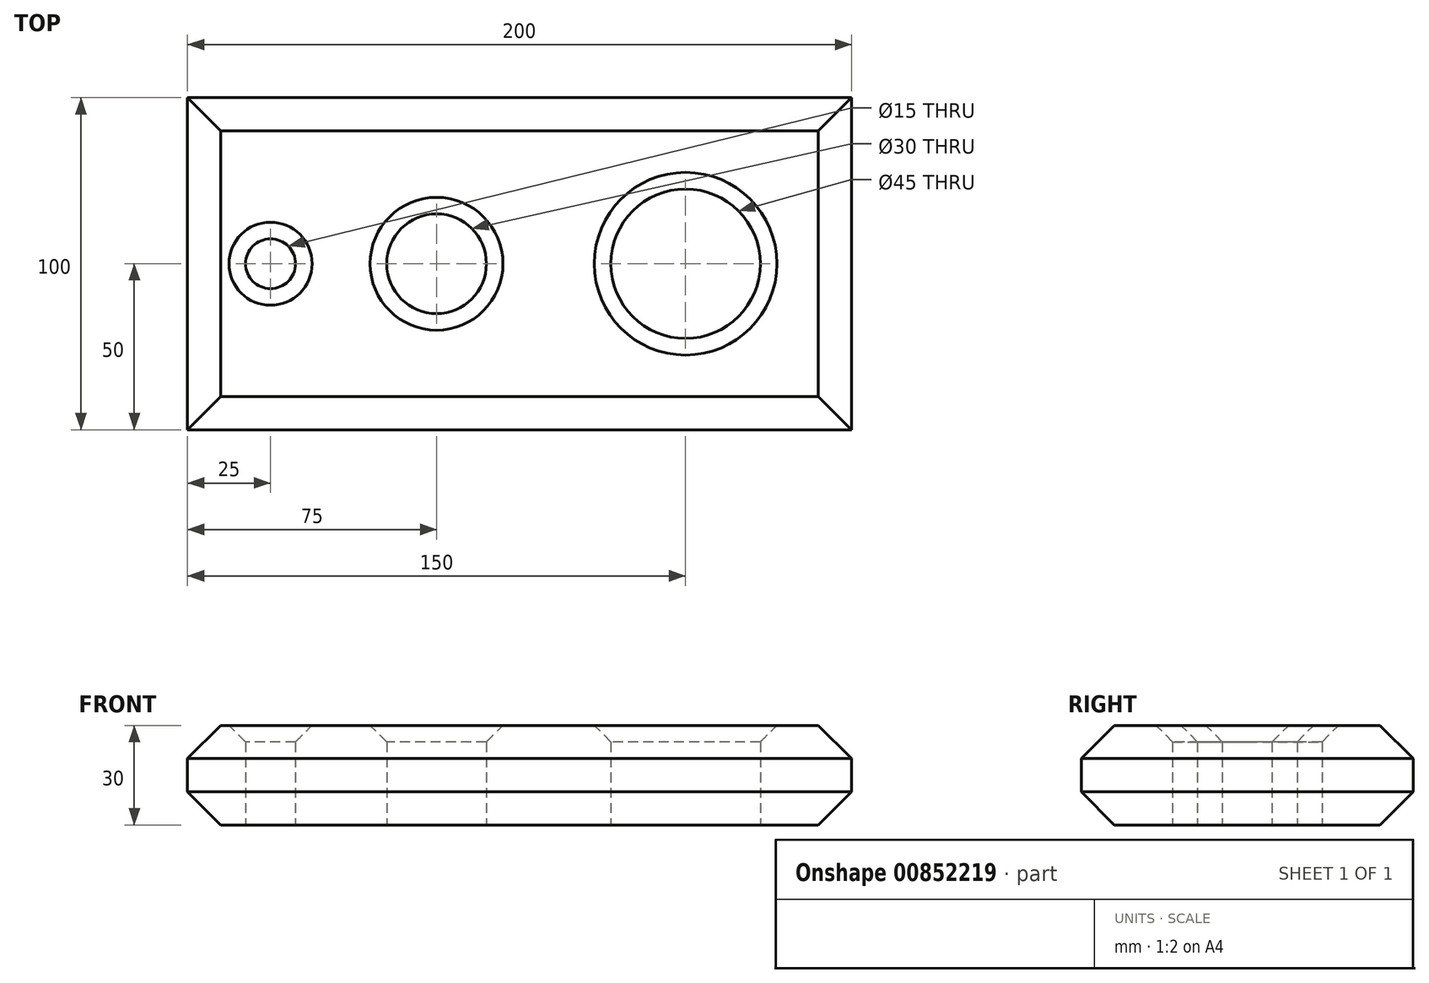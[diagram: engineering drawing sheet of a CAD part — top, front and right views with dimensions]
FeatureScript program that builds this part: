
annotation { "Feature Type Name" : "Feature", "Feature Type Description" : "" }
export const myFeature = defineFeature(function(context is Context, id is Id, definition is map)
    precondition{}
    {
        {
            var Q0;
            Q0=qCreatedBy(makeId("Top.planeOp"),FACE);
            var sketch = newSketch(context, id + "F0", { "sketchPlane" : qUnion([Q0])});
            skLineSegment(sketch, "E0.bottom", {"start": v(100, -50) * mm, "end": v(-100, -50) * mm});
            skLineSegment(sketch, "E0.top", {"start": v(100, 50) * mm, "end": v(-100, 50) * mm});
            skLineSegment(sketch, "E0.left", {"start": v(100, -50) * mm, "end": v(100, 50) * mm});
            skLineSegment(sketch, "E0.right", {"start": v(-100, -50) * mm, "end": v(-100, 50) * mm});
            skPoint(sketch, "E0.middle", {"position": v(0, 0) * mm});
            skCircle(sketch, "E1", {"center": v(-75, 0) * mm, "radius": 7.5 * mm});
            skCircle(sketch, "E2", {"center": v(-25, 0) * mm, "radius": 15 * mm});
            skCircle(sketch, "E3", {"center": v(50, 0) * mm, "radius": 22.5 * mm});
            skSolve(sketch);
        }
        {
            var Q0;
            Q0 = qSketchRegion(id + "F0", true);
            extrude(context, id + "F1", {"entities" : qUnion([Q0]), "depth" : 30 * mm, "offsetDistance" : 25 * mm});
        }
        {
            var Q0;
            Q0=makeQuery(id+"F1.opExtrude","CAP_EDGE",EDGE,{"disambiguationData":[OSD([sQuery(id+"F0.wireOp",EDGE,"E0.right")])],"isStart":false});
            var Q1;
            Q1=makeQuery(id+"F1.opExtrude","CAP_EDGE",EDGE,{"disambiguationData":[OSD([sQuery(id+"F0.wireOp",EDGE,"E0.bottom")])],"isStart":false});
            var Q2;
            Q2=makeQuery(id+"F1.opExtrude","CAP_EDGE",EDGE,{"disambiguationData":[OSD([sQuery(id+"F0.wireOp",EDGE,"E0.left")])],"isStart":false});
            var Q3;
            Q3=makeQuery(id+"F1.opExtrude","CAP_EDGE",EDGE,{"disambiguationData":[OSD([sQuery(id+"F0.wireOp",EDGE,"E0.top")])],"isStart":false});
            var Q4;
            Q4=makeQuery(id+"F1.opExtrude","CAP_EDGE",EDGE,{"disambiguationData":[OSD([sQuery(id+"F0.wireOp",EDGE,"E0.bottom")])],"isStart":true});
            var Q5;
            Q5=makeQuery(id+"F1.opExtrude","CAP_EDGE",EDGE,{"disambiguationData":[OSD([sQuery(id+"F0.wireOp",EDGE,"E0.right")])],"isStart":true});
            var Q6;
            Q6=makeQuery(id+"F1.opExtrude","CAP_EDGE",EDGE,{"disambiguationData":[OSD([sQuery(id+"F0.wireOp",EDGE,"E0.left")])],"isStart":true});
            var Q7;
            Q7=makeQuery(id+"F1.opExtrude","CAP_EDGE",EDGE,{"disambiguationData":[OSD([sQuery(id+"F0.wireOp",EDGE,"E0.top")])],"isStart":true});
            chamfer(context, id + "F2", {"entities" : qUnion([Q0, Q1, Q2, Q3, Q4, Q5, Q6, Q7]), "width" : 10 * mm, "tangentPropagation" : true});
        }
        {
            var Q0;
            Q0=makeQuery(id+"F1.opExtrude","CAP_EDGE",EDGE,{"disambiguationData":[OSD([sQuery(id+"F0.wireOp",EDGE,"E1")])],"isStart":false});
            var Q1;
            Q1=makeQuery(id+"F1.opExtrude","CAP_EDGE",EDGE,{"disambiguationData":[OSD([sQuery(id+"F0.wireOp",EDGE,"E2")])],"isStart":false});
            var Q2;
            Q2=makeQuery(id+"F1.opExtrude","CAP_EDGE",EDGE,{"disambiguationData":[OSD([sQuery(id+"F0.wireOp",EDGE,"E3")])],"isStart":false});
            chamfer(context, id + "F3", {"entities" : qUnion([Q0, Q1, Q2]), "width" : 5 * mm, "tangentPropagation" : true});
        }
    });
